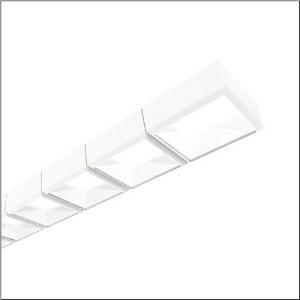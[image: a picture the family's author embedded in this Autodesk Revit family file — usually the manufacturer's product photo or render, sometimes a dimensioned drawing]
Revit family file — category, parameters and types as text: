
# Revit family: scriptus_r__11_5mz314d0twb_59a6
name_source: partatom
category: Lighting Fixtures
units: mm (PartAtom-declared; Revit-internal decimal feet)

## family parameters
Cut with Voids When Loaded = No
Host = Face
Light Source = No
Part Type = Normal
Room Calculation Point = No
Round Connector Dimension = Use Diameter
Shared = No

## types (1)
- --- (1 x LED 3000K+6500K / CRI = 80 (unbekannt), 3390 lm / 3600 lm, 3000K)
    Apparent Load = 106 VA
    CIE Flux Codes = 0 0 0 0 100 / 82 95 99 100 100
    Color Rendering = 80
    Color Temperature = 3000K
    Default Elevation = 1800 mm
    Description = Scriptus® 11, office luminaire, primary optical cover: lenses, CAT 2 (L<= 3000cd/m²), light emission: direct/indirect distribution, primary light characteristic: symmetric, installation type: suspended mounting, LED, rated luminous flux: 13.970lm, luminous efficacy: 128lm/W, light colour: 8tw, colour temperature: 3000..6500K, control gear: DALI DT8, with terminal, 5-pole, mains connection: 230V, AC, 50Hz, rated input power: 110W, LED, control gear: ECG DALI, housing, luminaire housing, of aluminium, traffic white (RAL 9016), length: 3.088mm, width: 114mm, height: 57mm, protection rating (complete): IP20, insulation class (complete): insulation class I (protective earthing), certification: CE, protection symbol: F, permissible operating ambient temperature: <= +25°C, standard: EN 50419, packaging unit: 1 piece
    Height = 57 mm
    Lamp = 1 x LED 3000K+6500K / CRI >= 80 (unbekannt)
    Lamp Light Flux = 3390 lm / 3600 lm
    Lamp count = 1
    Length = 3088 mm
    Luminous efficacy = 132 lm/W
    Manufacturer = Siteco
    ModVariant = No
    Model = 5MZ314D0TWB
    Mounting Place = Ceiling
    Mounting Type = Pendant
    Number of Poles = 1
    OnlyDefault = Yes
    Power Factor = 1
    Product Name = Scriptus® 11
    Product group = office luminaire | ceiling pendant
    ProductGroupID = 904
    Protection Class = Protection class I
    Protection Degree = IP 20
    RLX_Detail_Level = 1
    RLX_Emergency_Light_Flux = 0 lm
    RLX_Emergency_Type = 0
    RLX_Emergency_Type_DB = No
    RlxData = <blob elided: 32381 chars, md5=38a2cb4c>
    Socket = socket
    Standby Power = 0 W
    System Light Flux = 13980 lm
    System Power = 106 W
    Type Comments = individual setting: colour temperature 6500K
    Type Image = l_1004839.jpg
    URL = http://relux.com
    VarID = @adj_203039
    Voltage = 0 V
    Weight = 0.00 kg
    Width = 114 mm

## geometry (parser evidence)
native form markers: Blend x4, Sweep x19
no freeform markers — native parametric forms only
